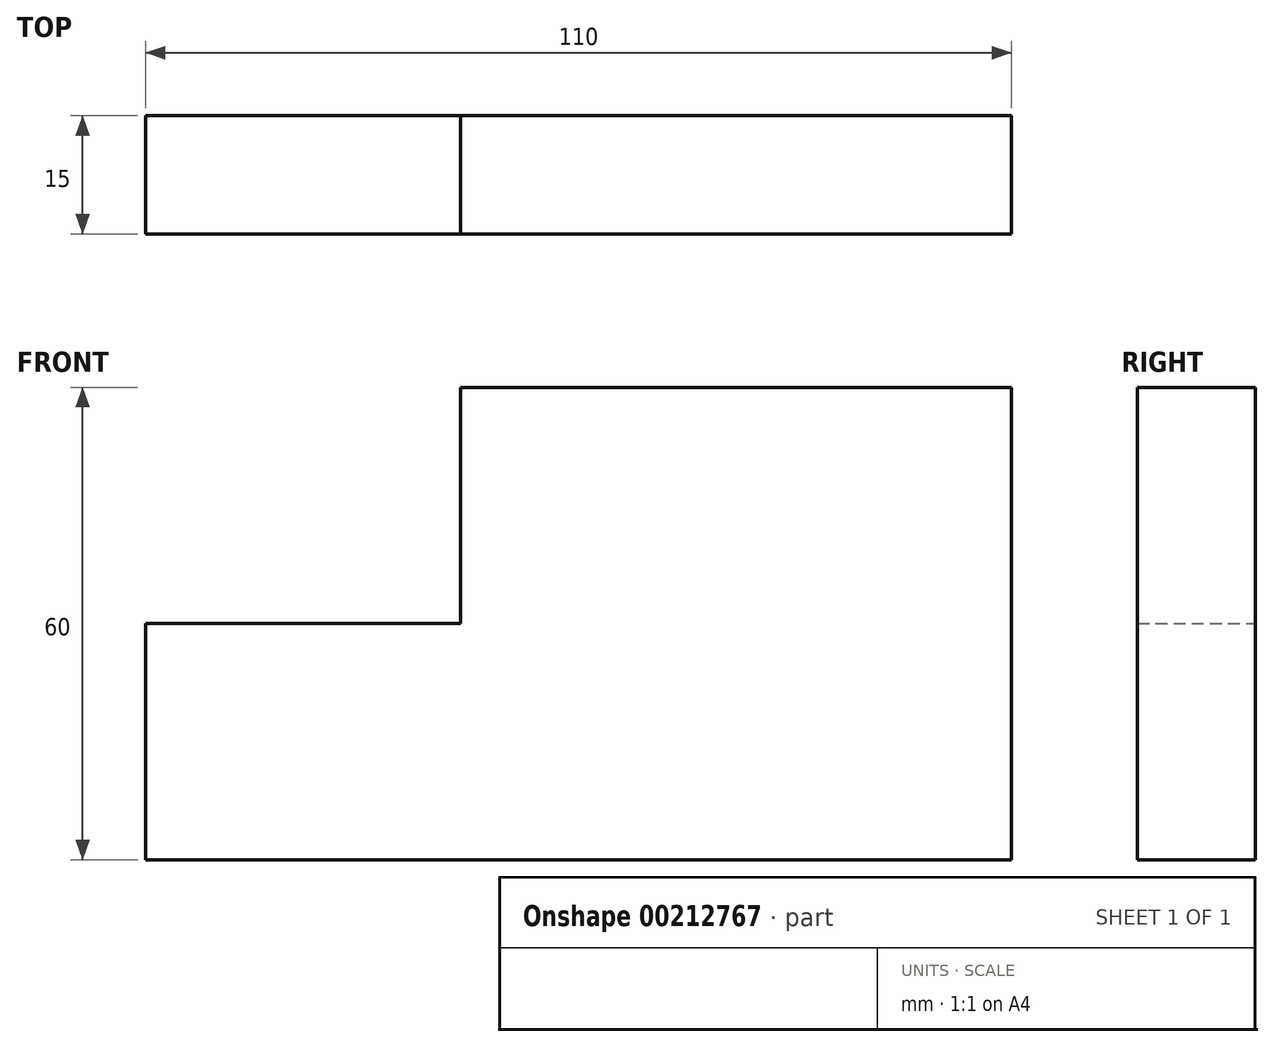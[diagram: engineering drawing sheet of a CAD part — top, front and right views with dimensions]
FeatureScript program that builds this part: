
annotation { "Feature Type Name" : "Feature", "Feature Type Description" : "" }
export const myFeature = defineFeature(function(context is Context, id is Id, definition is map)
    precondition{}
    {
        {
            var Q0;
            Q0=qCreatedBy(makeId("Front.planeOp"),FACE);
            var sketch = newSketch(context, id + "F0", { "sketchPlane" : qUnion([Q0])});
            skLineSegment(sketch, "E0", {"start": v(-64.72, 0) * mm, "end": v(-64.72, 30) * mm});
            skLineSegment(sketch, "E1", {"start": v(-64.72, 30) * mm, "end": v(-24.72, 30) * mm});
            skLineSegment(sketch, "E2", {"start": v(-24.72, 30) * mm, "end": v(-24.72, 60) * mm});
            skLineSegment(sketch, "E3", {"start": v(-24.72, 60) * mm, "end": v(45.28, 60) * mm});
            skLineSegment(sketch, "E4", {"start": v(45.28, 60) * mm, "end": v(45.28, 0) * mm});
            skLineSegment(sketch, "E5", {"start": v(45.28, 0) * mm, "end": v(-64.72, 0) * mm});
            skSolve(sketch);
        }
        {
            var Q0;
            Q0=makeQuery(id+"F0.imprint","IMPRINT",FACE,{"disambiguationData":[TD([[makeQuery(id+"F0.imprint","IMPRINT",EDGE,{"derivedFrom":sQuery(id+"F0.wireOp",EDGE,"E0")}),-1.0]])]});
            extrude(context, id + "F1", {"entities" : qUnion([Q0]), "endBound" : BoundingType.SYMMETRIC, "depth" : 15 * mm});
        }
    });
